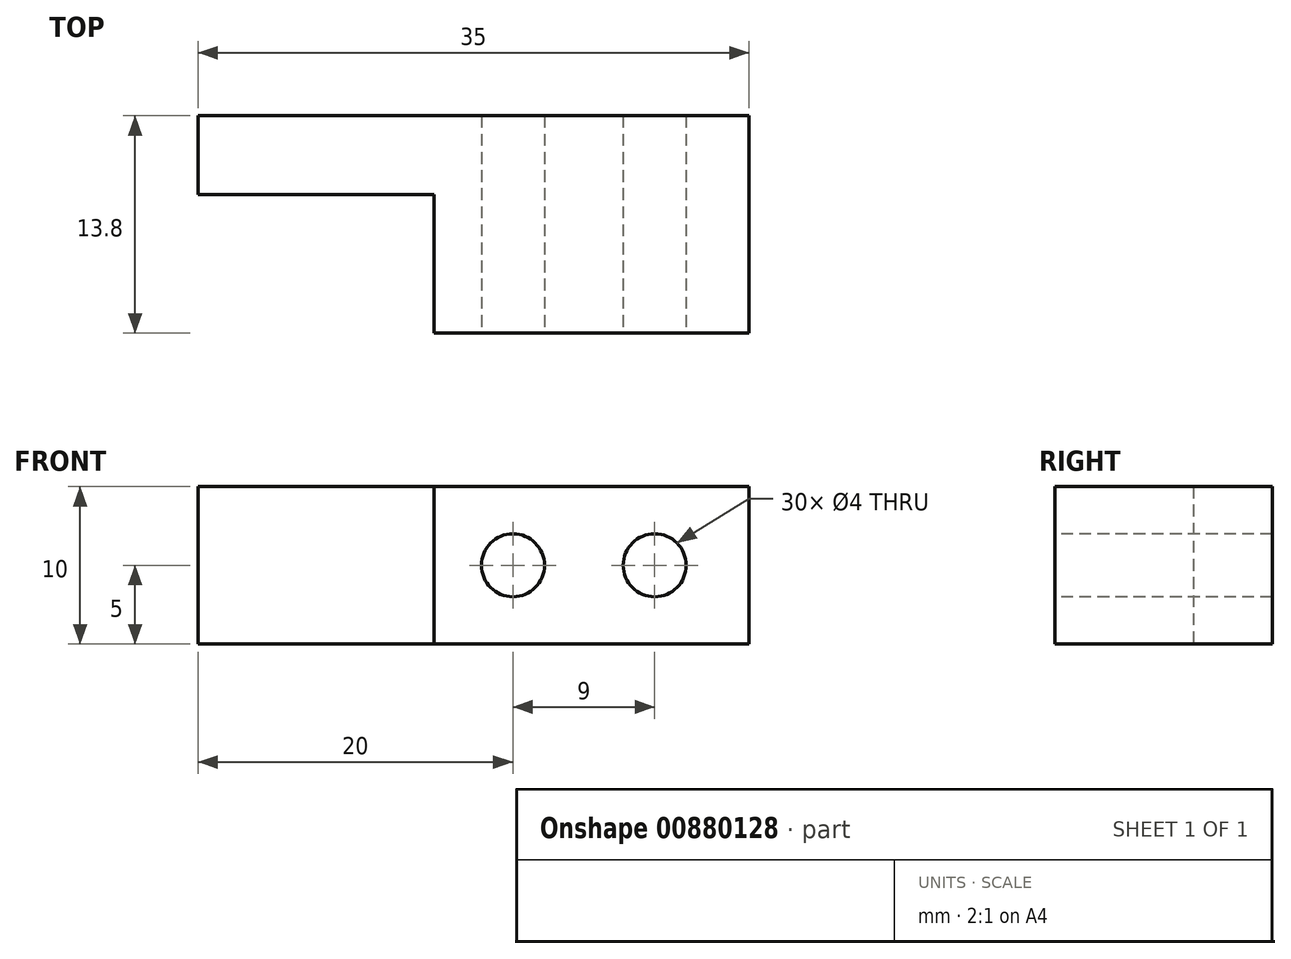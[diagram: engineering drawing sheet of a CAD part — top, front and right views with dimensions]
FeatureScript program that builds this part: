
annotation { "Feature Type Name" : "Feature", "Feature Type Description" : "" }
export const myFeature = defineFeature(function(context is Context, id is Id, definition is map)
    precondition{}
    {
        {
            var Q0;
            Q0=qCreatedBy(makeId("Front.planeOp"),FACE);
            var sketch = newSketch(context, id + "F0", { "sketchPlane" : qUnion([Q0])});
            skLineSegment(sketch, "E0.bottom", {"start": v(-17.5, 5) * mm, "end": v(17.5, 5) * mm});
            skLineSegment(sketch, "E0.top", {"start": v(-17.5, -5) * mm, "end": v(17.5, -5) * mm});
            skLineSegment(sketch, "E0.left", {"start": v(-17.5, 5) * mm, "end": v(-17.5, -5) * mm});
            skLineSegment(sketch, "E0.right", {"start": v(17.5, 5) * mm, "end": v(17.5, -5) * mm});
            skPoint(sketch, "E0.middle", {"position": v(0, 0) * mm});
            skSolve(sketch);
        }
        {
            var Q0;
            Q0=makeQuery(id+"F0.imprint","IMPRINT",FACE,{"disambiguationData":[TD([[makeQuery(id+"F0.imprint","IMPRINT",EDGE,{"derivedFrom":sQuery(id+"F0.wireOp",EDGE,"E0.bottom")}),-1.0]])]});
            extrude(context, id + "F1", {"entities" : qUnion([Q0]), "depth" : 13.8 * mm, "offsetDistance" : 25 * mm});
        }
        {
            var Q0;
            Q0=makeQuery(id+"F1.opExtrude","CAP_FACE",FACE,{"disambiguationData":[OSD([sQuery(id+"F0.wireOp",EDGE,"E0.bottom"),sQuery(id+"F0.wireOp",EDGE,"E0.top"),sQuery(id+"F0.wireOp",EDGE,"E0.left"),sQuery(id+"F0.wireOp",EDGE,"E0.right")])],"isStart":false});
            var sketch = newSketch(context, id + "F2", { "sketchPlane" : qUnion([Q0])});
            skLineSegment(sketch, "E1.bottom", {"start": v(-17.5, 5) * mm, "end": v(-2.5, 5) * mm});
            skLineSegment(sketch, "E1.top", {"start": v(-17.5, -5) * mm, "end": v(-2.5, -5) * mm});
            skLineSegment(sketch, "E1.left", {"start": v(-17.5, 5) * mm, "end": v(-17.5, -5) * mm});
            skLineSegment(sketch, "E1.right", {"start": v(-2.5, 5) * mm, "end": v(-2.5, -5) * mm});
            skSolve(sketch);
        }
        {
            var Q0;
            Q0=makeQuery(id+"F2.imprint","IMPRINT",FACE,{"disambiguationData":[TD([[makeQuery(id+"F2.imprint","IMPRINT",EDGE,{"derivedFrom":sQuery(id+"F2.wireOp",EDGE,"E1.bottom")}),-1.0]])]});
            extrude(context, id + "F3", {"entities" : qUnion([Q0]), "operationType" : NewBodyOperationType.REMOVE, "oppositeDirection" : true, "depth" : 8.8 * mm, "offsetDistance" : 25 * mm});
        }
        {
            var Q0;
            Q0=makeQuery(id+"F1.opExtrude","CAP_FACE",FACE,{"disambiguationData":[OSD([sQuery(id+"F0.wireOp",EDGE,"E0.bottom"),sQuery(id+"F0.wireOp",EDGE,"E0.top"),sQuery(id+"F0.wireOp",EDGE,"E0.left"),sQuery(id+"F0.wireOp",EDGE,"E0.right")])],"isStart":false});
            var sketch = newSketch(context, id + "F4", { "sketchPlane" : qUnion([Q0])});
            skCircle(sketch, "E2", {"center": v(2.5, 0) * mm, "radius": 2 * mm});
            skCircle(sketch, "E3", {"center": v(11.5, 0) * mm, "radius": 2 * mm});
            skSolve(sketch);
        }
        {
            var Q0;
            Q0=makeQuery(id+"F4.imprint","IMPRINT",FACE,{"disambiguationData":[TD([[makeQuery(id+"F4.imprint","IMPRINT",EDGE,{"derivedFrom":sQuery(id+"F4.wireOp",EDGE,"E2")}),1.0]])]});
            var Q1;
            Q1=makeQuery(id+"F4.imprint","IMPRINT",FACE,{"disambiguationData":[TD([[makeQuery(id+"F4.imprint","IMPRINT",EDGE,{"derivedFrom":sQuery(id+"F4.wireOp",EDGE,"E3")}),1.0]])]});
            extrude(context, id + "F5", {"entities" : qUnion([Q0, Q1]), "operationType" : NewBodyOperationType.REMOVE, "oppositeDirection" : true, "depth" : 13.8 * mm, "offsetDistance" : 25 * mm});
        }
    });
